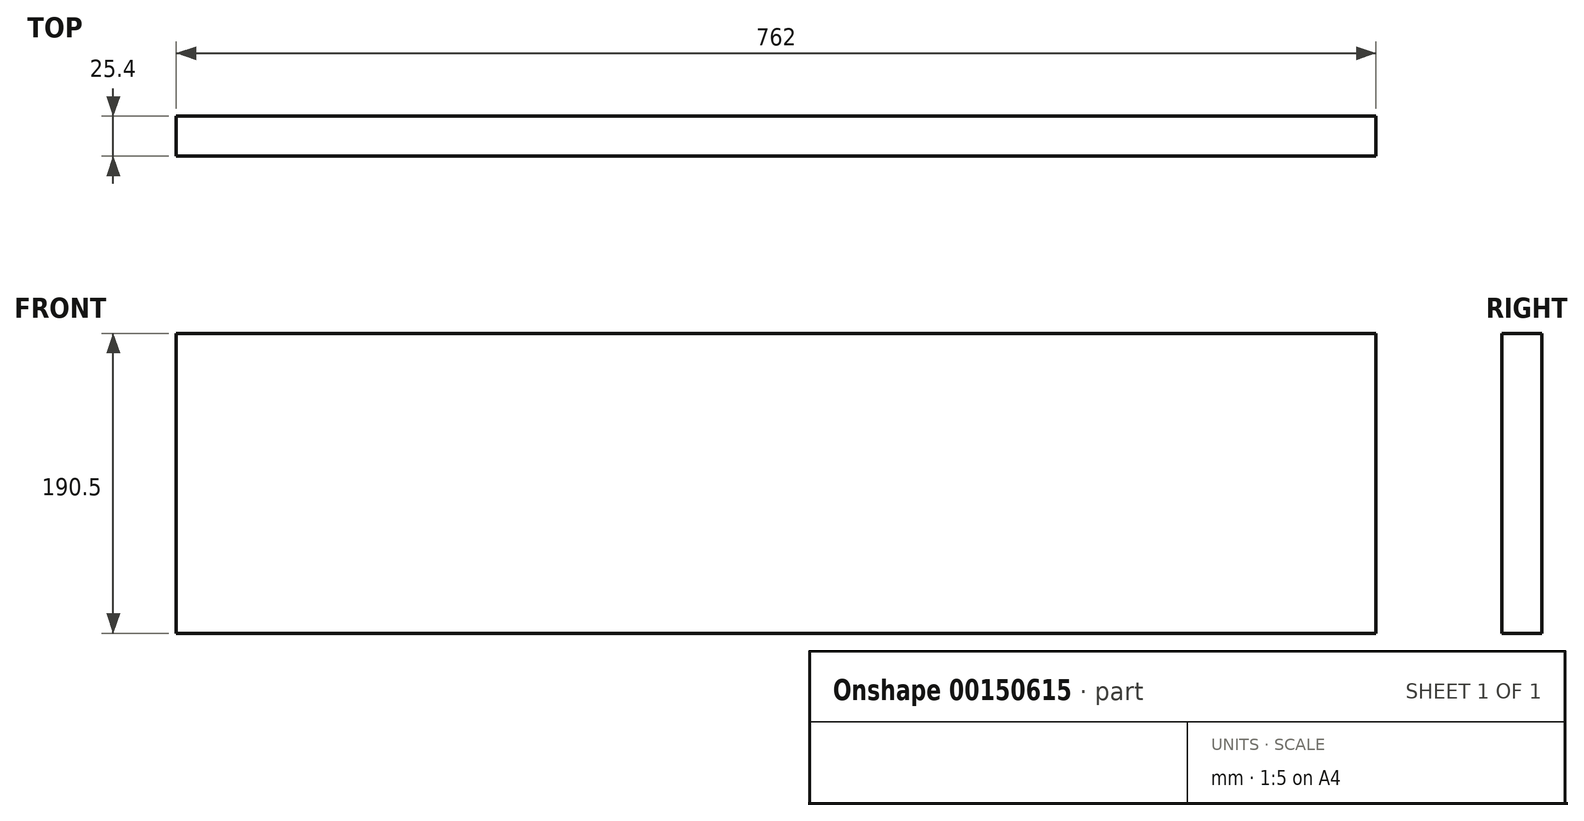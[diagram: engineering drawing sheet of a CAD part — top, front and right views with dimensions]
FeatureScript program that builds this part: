
annotation { "Feature Type Name" : "Feature", "Feature Type Description" : "" }
export const myFeature = defineFeature(function(context is Context, id is Id, definition is map)
    precondition{}
    {
        {
            var Q0;
            Q0=qCreatedBy(makeId("Front.planeOp"),FACE);
            var sketch = newSketch(context, id + "F0", { "sketchPlane" : qUnion([Q0])});
            skLineSegment(sketch, "E0", {"start": v(-150.02, 97.02) * mm, "end": v(-150.02, -93.48) * mm});
            skLineSegment(sketch, "E1", {"start": v(-150.02, 97.02) * mm, "end": v(611.98, 97.02) * mm});
            skLineSegment(sketch, "E2", {"start": v(611.98, 97.02) * mm, "end": v(611.98, -93.48) * mm});
            skLineSegment(sketch, "E3", {"start": v(-150.02, -93.48) * mm, "end": v(611.98, -93.48) * mm});
            skSolve(sketch);
        }
        {
            var Q0;
            Q0 = qSketchRegion(id + "F0", true);
            extrude(context, id + "F1", {"entities" : qUnion([Q0]), "depth" : 25.4 * mm});
        }
    });
